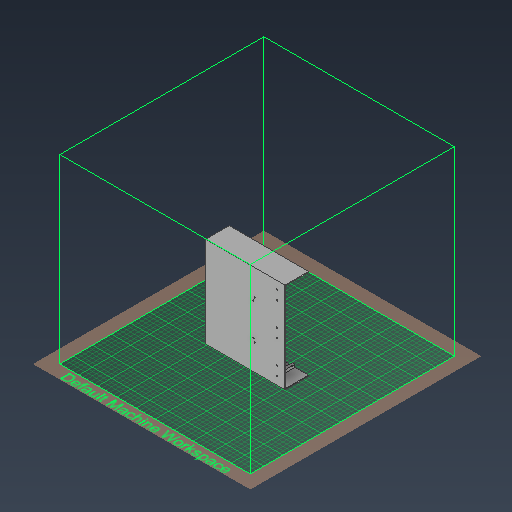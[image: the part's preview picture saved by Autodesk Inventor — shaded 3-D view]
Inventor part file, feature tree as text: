
AUTODESK INVENTOR PART (.ipt)
format: ipt  version: 2021 (Build 250183000, 183)  size: 577,024 bytes
history: native  units: mm
features: extrude x7, sketch x7, projected_geometry x6
ambient origin geometry x8: Origin, YZ Plane, XZ Plane, XY Plane, X Axis, Y Axis, Z Axis, Center Point
bodies: Volumenkörper1 (feature_tree)
feature tree (20):
  extrude  "Extrusion1"  Depth=200.0mm
  extrude  "Extrusion2"  Depth=2.0mm
  extrude  "Extrusion4"  Depth=17.5mm
  extrude  "Extrusion5"  Depth=20.0mm
  extrude  "Extrusion6"  Depth=2.0mm TaperAngle=0.0deg
  extrude  "Extrusion7"  Depth=2.0mm
  extrude  "Extrusion8"  Depth=6.0mm
  sketch  "Skizze1"  dims[d0=175.0mm d1=200.0mm]
  sketch  "Skizze2"  dims[d2=2.0mm d3=0.0mm d4=3.2mm]
  sketch  "Skizze4"  dims[d5=17.5mm d6=17.5mm]
  sketch  "Skizze5"  dims[d7=3.2mm d8=20.0mm]
  sketch  "Skizze6"  dims[d9=17.5mm d10=2.0mm d11=0.0mm]
  sketch  "Skizze7"  dims[d18=2.0mm d19=2.0mm]
  sketch  "Skizze8"  dims[d21=6.0mm d23=6.0mm d24=2.0mm d25=6.0mm d26=6.0mm d27=6.0mm d28=6.0mm d29=50.0mm d30=0.0mm d31=7.0mm d32=7.0mm d35=20.0mm d36=20.0mm d37=7.0mm d38=73.0mm d40=7.0mm d42=73.0mm d43=7.0mm d44=0.0mm d45=4.0mm d46=4.0mm d47=4.0mm d48=0.0mm d49=4.0mm d50=73.0mm d51=70.0mm d52=5.0mm d53=0.0mm d54=4.0mm d55=4.0mm d56=4.0mm d57=4.0mm d59=3.0mm d61=3.0mm d62=3.0mm d63=3.0mm d64=3.0mm d65=3.0mm d66=5.0mm d67=0.0mm d68=70.0mm d69=70.0mm d70=35.0mm d73=65.0mm d74=7.0mm d75=7.0mm d83=7.0mm d86=7.0mm d96=4.0mm d97=0.0mm d98=0.0mm d99=4.0mm d100=0.0mm d101=0.0mm d102=4.0mm d103=0.0mm d104=4.0mm d105=0.0mm d119=3.2mm d120=18.0mm d121=10.0mm d122=3.2mm d123=3.2mm d124=66.891mm d125=69.627mm d126=42.961mm d127=35.444mm d128=10.0mm d129=0.0mm d130=6.0mm d131=30.0mm d132=6.0mm d133=30.0mm d136=48.26mm d137=74.93mm d138=48.26mm d139=82.55mm d142=30.0mm d143=30.0mm d144=34.225mm d145=47.055mm d146=3.0mm d147=3.0mm d148=7.0mm d149=7.0mm d150=7.0mm d151=7.0mm d152=10.0mm d153=10.0mm d154=39.0mm d155=39.0mm d156=51.0mm d157=51.0mm d161=7.5mm d163=7.5mm d164=7.0mm d165=0.0mm d166=0.0mm d167=4.0mm d168=7.0mm d169=0.0mm d170=4.0mm d171=4.0mm d172=0.0mm d173=7.0mm d174=7.0mm d176=4.0mm d177=7.0mm d178=7.0mm d179=7.0mm d180=7.0mm d181=10.0mm d182=10.0mm d183=7.5mm d184=34.0mm d185=7.5mm d186=34.0mm d187=54.0mm d188=54.0mm d189=4.0mm d190=4.0mm d191=4.0mm d192=4.0mm d193=7.0mm d194=25.0mm d195=9.0mm d196=7.0mm d197=25.0mm d198=9.0mm d199=4.0mm d200=4.0mm]
  projected_geometry  "Projizierte Kontur1"
  projected_geometry  "Projizierte Kontur2"
  projected_geometry  "Projizierte Kontur3"
  projected_geometry  "Projizierte Kontur4"
  projected_geometry  "Projizierte Kontur5"
  projected_geometry  "Projizierte Kontur6"
